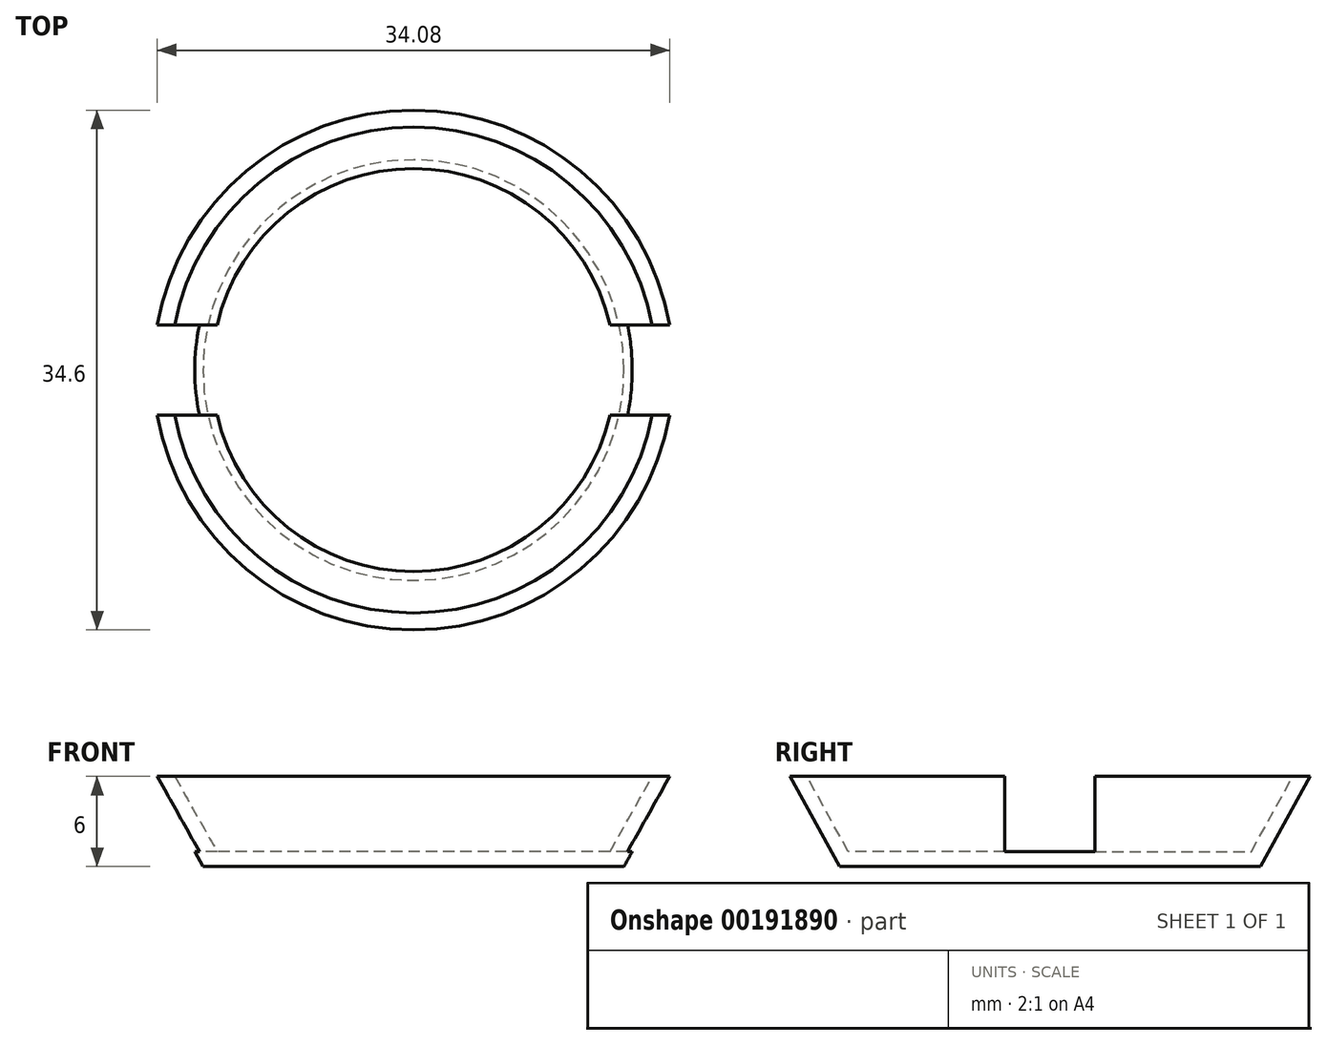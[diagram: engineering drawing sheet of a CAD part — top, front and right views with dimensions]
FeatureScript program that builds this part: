
annotation { "Feature Type Name" : "Feature", "Feature Type Description" : "" }
export const myFeature = defineFeature(function(context is Context, id is Id, definition is map)
    precondition{}
    {
        {
            var Q0;
            Q0=qCreatedBy(makeId("Right.planeOp"),FACE);
            var sketch = newSketch(context, id + "F0", { "sketchPlane" : qUnion([Q0])});
            skLineSegment(sketch, "E0", {"start": v(0, 0) * mm, "end": v(14, 0) * mm});
            skLineSegment(sketch, "E1", {"start": v(14, 0) * mm, "end": v(17.3, 6) * mm});
            skLineSegment(sketch, "E2", {"start": v(17.3, 6) * mm, "end": v(0, 6) * mm});
            skLineSegment(sketch, "E3", {"start": v(0, 6) * mm, "end": v(0, 0) * mm});
            skSolve(sketch);
        }
        {
            var Q0;
            Q0=makeQuery(id+"F0.imprint","IMPRINT",FACE,{"disambiguationData":[TD([[makeQuery(id+"F0.imprint","IMPRINT",EDGE,{"derivedFrom":sQuery(id+"F0.wireOp",EDGE,"E0")}),1.0]])]});
            var Q1;
            Q1=sQuery(id+"F0.wireOp",EDGE,"E3");
            revolve(context, id + "F1", {"entities" : qUnion([Q0]), "axis" : qUnion([Q1]), "revolveType" : RevolveType.FULL});
        }
        {
            var Q0;
            Q0=makeQuery(id+"F1.opRevolve","SWEPT_FACE",FACE,{"disambiguationData":[OSD([sQuery(id+"F0.wireOp",EDGE,"E2")])]});
            shell(context, id + "F2", {"entities" : qUnion([Q0]), "thickness" : 1 * mm});
        }
        {
            var Q0;
            Q0=makeQuery(id+"F2.opShell","OFFSET_FACE",FACE,{"disambiguationData":[OSD([sQuery(id+"F0.wireOp",EDGE,"E0")])]});
            var sketch = newSketch(context, id + "F3", { "sketchPlane" : qUnion([Q0])});
            skLineSegment(sketch, "E4.bottom", {"start": v(25, -3) * mm, "end": v(-25, -3) * mm});
            skLineSegment(sketch, "E4.top", {"start": v(25, 3) * mm, "end": v(-25, 3) * mm});
            skLineSegment(sketch, "E4.left", {"start": v(25, -3) * mm, "end": v(25, 3) * mm});
            skLineSegment(sketch, "E4.right", {"start": v(-25, -3) * mm, "end": v(-25, 3) * mm});
            skPoint(sketch, "E4.middle", {"position": v(0, 0) * mm});
            skSolve(sketch);
        }
        {
            var Q0;
            {var subQ0=sQuery(id+"F3.wireOp",EDGE,"E4.left");Q0=makeQuery(id+"F3.imprint","IMPRINT",FACE,{"disambiguationData":[TD([[makeQuery(id+"F3.imprint","IMPRINT",EDGE,{"derivedFrom":subQ0}),1.0]])]});}
            var Q1;
            {var subQ0=sQuery(id+"F3.wireOp",EDGE,"E4.right");Q1=makeQuery(id+"F3.imprint","IMPRINT",FACE,{"disambiguationData":[TD([[makeQuery(id+"F3.imprint","IMPRINT",EDGE,{"derivedFrom":subQ0}),-1.0]])]});}
            var Q2;
            {var subQ0=sQuery(id+"F3.wireOp",EDGE,"E4.bottom");var subQ1=makeQuery(id+"F2.opShell","OFFSET_EDGE",EDGE,{"disambiguationData":[OSD([sQuery(id+"F0.wireOp",EDGE,"E0"),sQuery(id+"F0.wireOp",EDGE,"E1")])]});var subQ2=makeQuery(id+"F3.imprint","INTERSECT",VERTEX,{"disambiguationData":[OD(0.0)],"derivedFrom":[subQ1,subQ0]});Q2=makeQuery(id+"F3.imprint","IMPRINT",FACE,{"disambiguationData":[TD([[makeQuery(id+"F3.imprint","IMPRINT",EDGE,{"disambiguationData":[TD([[subQ2,-1.0]])],"derivedFrom":subQ0}),-1.0]])]});}
            extrude(context, id + "F4", {"entities" : qUnion([Q0, Q1, Q2]), "operationType" : NewBodyOperationType.REMOVE, "endBound" : BoundingType.THROUGH_ALL, "depth" : 25 * mm});
        }
    });
